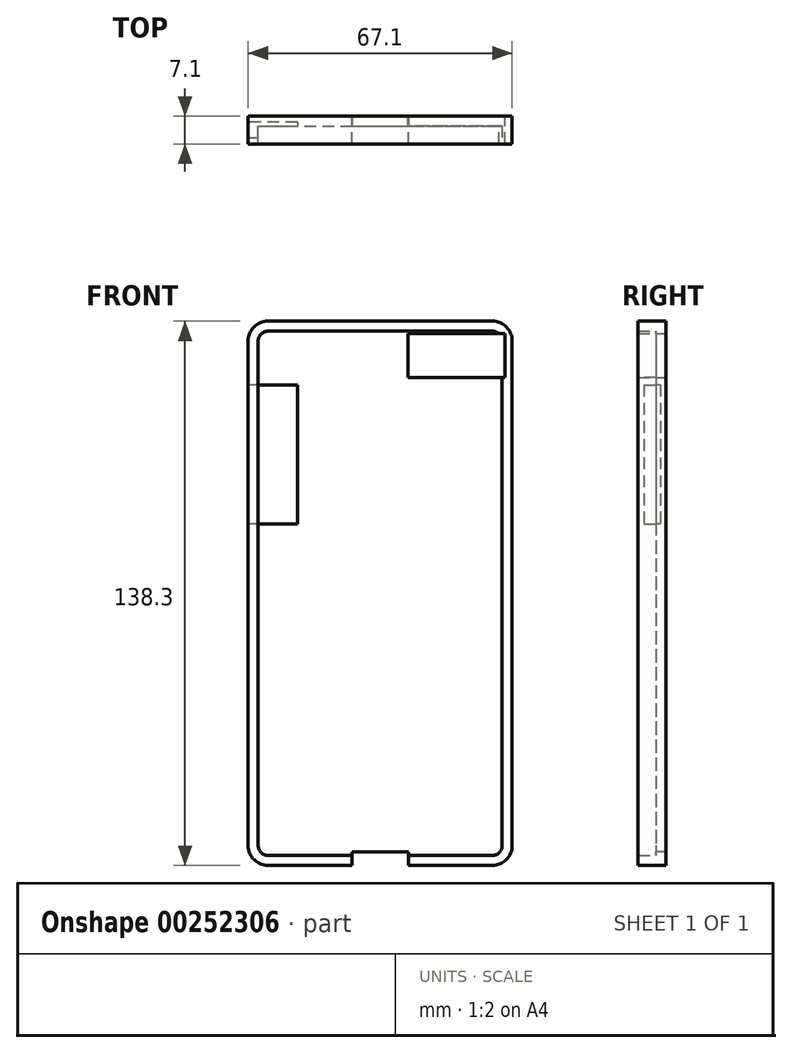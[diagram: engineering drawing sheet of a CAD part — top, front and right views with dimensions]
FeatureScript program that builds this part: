
annotation { "Feature Type Name" : "Feature", "Feature Type Description" : "" }
export const myFeature = defineFeature(function(context is Context, id is Id, definition is map)
    precondition{}
    {
        {
            var Q0;
            Q0=qCreatedBy(makeId("Front.planeOp"),FACE);
            var sketch = newSketch(context, id + "F0", { "sketchPlane" : qUnion([Q0])});
            skLineSegment(sketch, "E0.bottom", {"start": v(-33.55, 69.15) * mm, "end": v(33.55, 69.15) * mm});
            skLineSegment(sketch, "E0.top", {"start": v(-33.55, -69.15) * mm, "end": v(33.55, -69.15) * mm});
            skLineSegment(sketch, "E0.left", {"start": v(-33.55, 69.15) * mm, "end": v(-33.55, -69.15) * mm});
            skLineSegment(sketch, "E0.right", {"start": v(33.55, 69.15) * mm, "end": v(33.55, -69.15) * mm});
            skPoint(sketch, "E0.middle", {"position": v(0, 0) * mm});
            skSolve(sketch);
        }
        {
            var Q0;
            Q0=makeQuery(id+"F0.imprint","IMPRINT",FACE,{"disambiguationData":[TD([[makeQuery(id+"F0.imprint","IMPRINT",EDGE,{"derivedFrom":sQuery(id+"F0.wireOp",EDGE,"E0.bottom")}),-1.0]])]});
            extrude(context, id + "F1", {"entities" : qUnion([Q0]), "endBound" : BoundingType.SYMMETRIC, "depth" : 7.1 * mm});
        }
        {
            var Q0;
            Q0=makeQuery(id+"F1.opExtrude","SWEPT_EDGE",EDGE,{"disambiguationData":[OSD([sQuery(id+"F0.wireOp",EDGE,"E0.bottom"),sQuery(id+"F0.wireOp",EDGE,"E0.left")])]});
            var Q1;
            Q1=makeQuery(id+"F1.opExtrude","SWEPT_EDGE",EDGE,{"disambiguationData":[OSD([sQuery(id+"F0.wireOp",EDGE,"E0.bottom"),sQuery(id+"F0.wireOp",EDGE,"E0.right")])]});
            var Q2;
            Q2=makeQuery(id+"F1.opExtrude","SWEPT_EDGE",EDGE,{"disambiguationData":[OSD([sQuery(id+"F0.wireOp",EDGE,"E0.top"),sQuery(id+"F0.wireOp",EDGE,"E0.right")])]});
            var Q3;
            Q3=makeQuery(id+"F1.opExtrude","SWEPT_EDGE",EDGE,{"disambiguationData":[OSD([sQuery(id+"F0.wireOp",EDGE,"E0.top"),sQuery(id+"F0.wireOp",EDGE,"E0.left")])]});
            fillet(context, id + "F2", {"entities" : qUnion([Q0, Q1, Q2, Q3]), "radius" : 5.08 * mm, "tangentPropagation" : true, "allowEdgeOverflow" : false});
        }
        {
            var Q0;
            Q0=makeQuery(id+"F1.opExtrude","CAP_FACE",FACE,{"disambiguationData":[OSD([sQuery(id+"F0.wireOp",EDGE,"E0.bottom"),sQuery(id+"F0.wireOp",EDGE,"E0.top"),sQuery(id+"F0.wireOp",EDGE,"E0.left"),sQuery(id+"F0.wireOp",EDGE,"E0.right")])],"isStart":false});
            shell(context, id + "F3", {"entities" : qUnion([Q0]), "thickness" : 2.54 * mm});
        }
        {
            var Q0;
            Q0=makeQuery(id+"F1.opExtrude","CAP_FACE",FACE,{"disambiguationData":[OSD([sQuery(id+"F0.wireOp",EDGE,"E0.bottom"),sQuery(id+"F0.wireOp",EDGE,"E0.top"),sQuery(id+"F0.wireOp",EDGE,"E0.left"),sQuery(id+"F0.wireOp",EDGE,"E0.right")])],"isStart":true});
            var sketch = newSketch(context, id + "F4", { "sketchPlane" : qUnion([Q0])});
            skLineSegment(sketch, "E1.bottom", {"start": v(-7.01, 54.84) * mm, "end": v(-31.65, 54.84) * mm});
            skLineSegment(sketch, "E1.top", {"start": v(-7.01, 65.99) * mm, "end": v(-31.65, 65.99) * mm});
            skLineSegment(sketch, "E1.left", {"start": v(-7.01, 54.84) * mm, "end": v(-7.01, 65.99) * mm});
            skLineSegment(sketch, "E1.right", {"start": v(-31.65, 54.84) * mm, "end": v(-31.65, 65.99) * mm});
            skPoint(sketch, "E1.middle", {"position": v(-19.33, 60.42) * mm});
            skSolve(sketch);
        }
        {
            var Q0;
            Q0=makeQuery(id+"F4.imprint","IMPRINT",FACE,{"disambiguationData":[TD([[makeQuery(id+"F4.imprint","IMPRINT",EDGE,{"derivedFrom":sQuery(id+"F4.wireOp",EDGE,"E1.bottom")}),-1.0]])]});
            extrude(context, id + "F5", {"entities" : qUnion([Q0]), "operationType" : NewBodyOperationType.REMOVE, "endBound" : BoundingType.SYMMETRIC, "oppositeDirection" : true, "depth" : 25 * mm});
        }
        {
            var Q0;
            Q0=makeQuery(id+"F1.opExtrude","SWEPT_FACE",FACE,{"disambiguationData":[OSD([sQuery(id+"F0.wireOp",EDGE,"E0.top")])]});
            var sketch = newSketch(context, id + "F6", { "sketchPlane" : qUnion([Q0])});
            skLineSegment(sketch, "E2.bottom", {"start": v(7.17, -3.55) * mm, "end": v(-7.17, -3.55) * mm});
            skLineSegment(sketch, "E2.top", {"start": v(7.17, 3.55) * mm, "end": v(-7.17, 3.55) * mm});
            skLineSegment(sketch, "E2.left", {"start": v(7.17, -3.55) * mm, "end": v(7.17, 3.55) * mm});
            skLineSegment(sketch, "E2.right", {"start": v(-7.17, -3.55) * mm, "end": v(-7.17, 3.55) * mm});
            skPoint(sketch, "E2.middle", {"position": v(0, 0) * mm});
            skSolve(sketch);
        }
        {
            var Q0;
            Q0=makeQuery(id+"F6.imprint","IMPRINT",FACE,{"disambiguationData":[TD([[makeQuery(id+"F6.imprint","IMPRINT",EDGE,{"derivedFrom":sQuery(id+"F6.wireOp",EDGE,"E2.bottom")}),1.0]])]});
            extrude(context, id + "F7", {"entities" : qUnion([Q0]), "operationType" : NewBodyOperationType.REMOVE, "endBound" : BoundingType.SYMMETRIC, "oppositeDirection" : true, "depth" : 7 * mm});
        }
        {
            var Q0;
            Q0=makeQuery(id+"F1.opExtrude","SWEPT_FACE",FACE,{"disambiguationData":[OSD([sQuery(id+"F0.wireOp",EDGE,"E0.left")])]});
            var sketch = newSketch(context, id + "F8", { "sketchPlane" : qUnion([Q0])});
            skLineSegment(sketch, "E3.bottom", {"start": v(-2.06, 17.64) * mm, "end": v(2.06, 17.64) * mm});
            skLineSegment(sketch, "E3.top", {"start": v(-2.06, 52.96) * mm, "end": v(2.06, 52.96) * mm});
            skLineSegment(sketch, "E3.left", {"start": v(-2.06, 17.64) * mm, "end": v(-2.06, 52.96) * mm});
            skLineSegment(sketch, "E3.right", {"start": v(2.06, 17.64) * mm, "end": v(2.06, 52.96) * mm});
            skPoint(sketch, "E3.middle", {"position": v(0, 35.3) * mm});
            skSolve(sketch);
        }
        {
            var Q0;
            Q0=makeQuery(id+"F8.imprint","IMPRINT",FACE,{"disambiguationData":[TD([[makeQuery(id+"F8.imprint","IMPRINT",EDGE,{"derivedFrom":sQuery(id+"F8.wireOp",EDGE,"E3.bottom")}),1.0]])]});
            extrude(context, id + "F9", {"entities" : qUnion([Q0]), "operationType" : NewBodyOperationType.REMOVE, "endBound" : BoundingType.SYMMETRIC, "oppositeDirection" : true, "depth" : 25 * mm});
        }
    });
